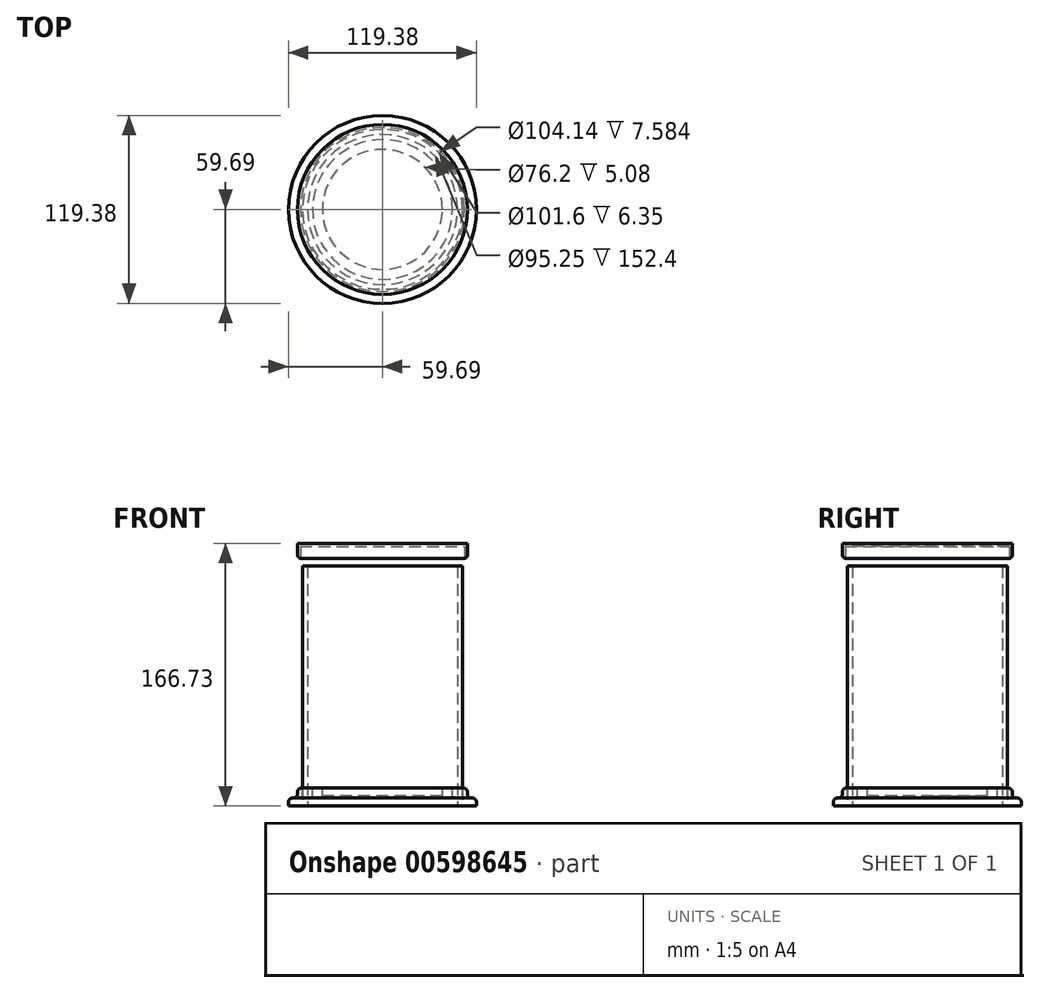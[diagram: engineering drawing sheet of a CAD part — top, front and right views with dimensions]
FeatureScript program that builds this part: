
annotation { "Feature Type Name" : "Feature", "Feature Type Description" : "" }
export const myFeature = defineFeature(function(context is Context, id is Id, definition is map)
    precondition{}
    {
        {
            var Q0;
            Q0=qCreatedBy(makeId("Top.planeOp"),FACE);
            var sketch = newSketch(context, id + "F0", { "sketchPlane" : qUnion([Q0])});
            skCircle(sketch, "E0", {"center": v(0, 0) * mm, "radius": 50.8 * mm});
            skCircle(sketch, "E1", {"center": v(0, 0) * mm, "radius": 47.63 * mm});
            skSolve(sketch);
        }
        {
            var Q0;
            Q0 = qSketchRegion(id + "F0", true);
            extrude(context, id + "F1", {"entities" : qUnion([Q0]), "depth" : 152.4 * mm, "offsetDistance" : 25 * mm});
        }
        {
            var Q0;
            Q0=qCreatedBy(makeId("Front.planeOp"),FACE);
            var sketch = newSketch(context, id + "F2", { "sketchPlane" : qUnion([Q0])});
            skLineSegment(sketch, "E2", {"start": v(0, 0) * mm, "end": v(59.7, 0) * mm});
            skLineSegment(sketch, "E3", {"start": v(59.7, 0) * mm, "end": v(59.7, 2.54) * mm});
            skLineSegment(sketch, "E4", {"start": v(57.15, 5.08) * mm, "end": v(56.52, 5.08) * mm});
            skLineSegment(sketch, "E5", {"start": v(53.98, 7.62) * mm, "end": v(53.98, 8.9) * mm});
            skLineSegment(sketch, "E6", {"start": v(51.44, 11.43) * mm, "end": v(50.8, 11.43) * mm});
            skLineSegment(sketch, "E7", {"start": v(50.8, 11.43) * mm, "end": v(50.8, 5.08) * mm});
            skLineSegment(sketch, "E8", {"start": v(50.8, 5.08) * mm, "end": v(44.45, 5.08) * mm});
            skLineSegment(sketch, "E9", {"start": v(44.45, 5.08) * mm, "end": v(44.45, 11.43) * mm});
            skLineSegment(sketch, "E10", {"start": v(0, 6.35) * mm, "end": v(0, 0) * mm});
            skLineSegment(sketch, "E11", {"start": v(0, 6.35) * mm, "end": v(38.1, 6.35) * mm});
            skLineSegment(sketch, "E12", {"start": v(38.1, 6.35) * mm, "end": v(38.1, 11.43) * mm});
            skLineSegment(sketch, "E13", {"start": v(38.1, 11.43) * mm, "end": v(44.45, 11.43) * mm});
            skPoint(sketch, "E14.visualSharp", {"position": v(59.7, 5.08) * mm});
            skArc(sketch, "E14.filletArc", {"start": v(59.7, 2.54) * mm, "mid": v(58.95, 4.34) * mm, "end": v(57.15, 5.08) * mm});
            skPoint(sketch, "E15.visualSharp", {"position": v(53.98, 11.43) * mm});
            skArc(sketch, "E15.filletArc", {"start": v(53.98, 8.9) * mm, "mid": v(53.23, 10.69) * mm, "end": v(51.44, 11.43) * mm});
            skPoint(sketch, "E16.visualSharp", {"position": v(53.98, 5.08) * mm});
            skArc(sketch, "E16.filletArc", {"start": v(53.98, 7.62) * mm, "mid": v(54.72, 5.82) * mm, "end": v(56.52, 5.08) * mm});
            skSolve(sketch);
        }
        {
            var Q0;
            Q0 = qSketchRegion(id + "F2", true);
            var Q1;
            Q1=sQuery(id+"F2.wireOp",EDGE,"E10");
            revolve(context, id + "F3", {"entities" : qUnion([Q0]), "axis" : qUnion([Q1]), "revolveType" : RevolveType.FULL});
        }
        {
            var Q0;
            Q0=qCreatedBy(makeId("Front.planeOp"),FACE);
            var sketch = newSketch(context, id + "F4", { "sketchPlane" : qUnion([Q0])});
            skLineSegment(sketch, "E17", {"start": v(0, 166.73) * mm, "end": v(53.98, 166.73) * mm});
            skLineSegment(sketch, "E18", {"start": v(53.98, 166.73) * mm, "end": v(53.98, 157.24) * mm});
            skLineSegment(sketch, "E19", {"start": v(53.98, 157.24) * mm, "end": v(52.07, 157.24) * mm});
            skLineSegment(sketch, "E20", {"start": v(52.07, 157.24) * mm, "end": v(52.07, 164.82) * mm});
            skLineSegment(sketch, "E21", {"start": v(52.07, 164.82) * mm, "end": v(0, 164.82) * mm});
            skLineSegment(sketch, "E22", {"start": v(0, 164.82) * mm, "end": v(0, 166.73) * mm});
            skSolve(sketch);
        }
        {
            var Q0;
            Q0=makeQuery(id+"F4.imprint","IMPRINT",FACE,{"disambiguationData":[TD([[makeQuery(id+"F4.imprint","IMPRINT",EDGE,{"derivedFrom":sQuery(id+"F4.wireOp",EDGE,"E17")}),-1.0]])]});
            var Q1;
            Q1=sQuery(id+"F4.wireOp",EDGE,"E22");
            revolve(context, id + "F5", {"entities" : qUnion([Q0]), "axis" : qUnion([Q1]), "revolveType" : RevolveType.FULL});
        }
        {
            var Q0;
            Q0=makeQuery(id+"F5.opRevolve","SWEPT_EDGE",EDGE,{"disambiguationData":[OSD([sQuery(id+"F4.wireOp",EDGE,"E18"),sQuery(id+"F4.wireOp",EDGE,"E19")])]});
            fillet(context, id + "F6", {"entities" : qUnion([Q0]), "radius" : 2.54 * mm, "tangentPropagation" : true, "allowEdgeOverflow" : false});
        }
    });
